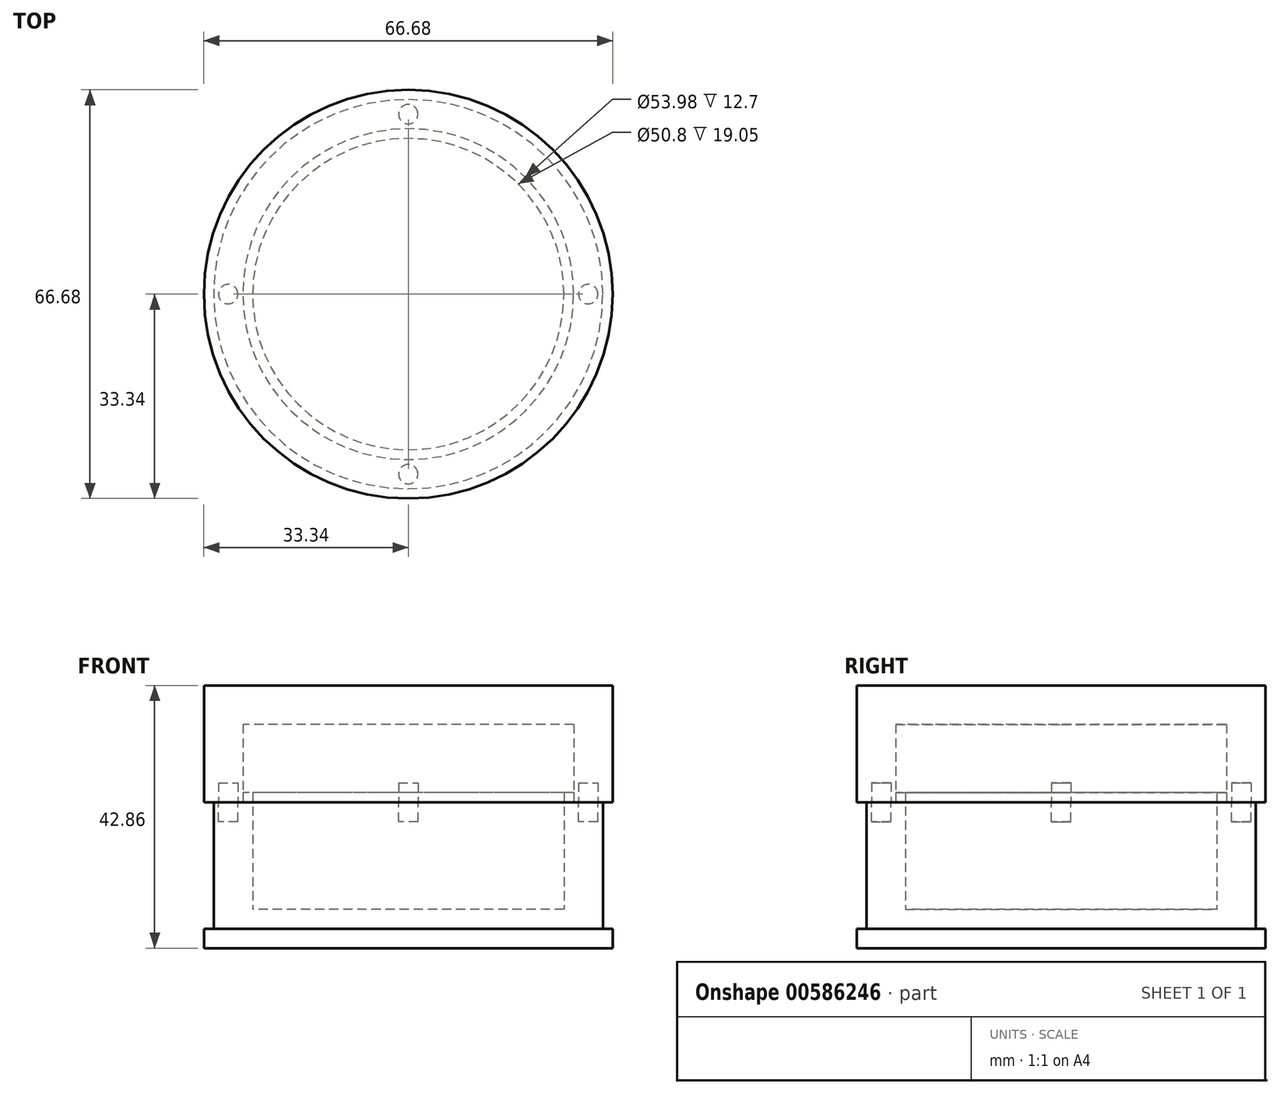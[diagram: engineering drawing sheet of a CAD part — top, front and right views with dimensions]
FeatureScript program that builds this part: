
annotation { "Feature Type Name" : "Feature", "Feature Type Description" : "" }
export const myFeature = defineFeature(function(context is Context, id is Id, definition is map)
    precondition{}
    {
        {
            var Q0;
            Q0=qCreatedBy(makeId("Top.planeOp"),FACE);
            var sketch = newSketch(context, id + "F0", { "sketchPlane" : qUnion([Q0])});
            skCircle(sketch, "E0", {"center": v(0, 0) * mm, "radius": 31.75 * mm});
            skCircle(sketch, "E1", {"center": v(0, 0) * mm, "radius": 33.34 * mm});
            skCircle(sketch, "E2", {"center": v(0, 0) * mm, "radius": 25.4 * mm});
            skSolve(sketch);
        }
        {
            var Q0;
            Q0=makeQuery(id+"F0.imprint","IMPRINT",FACE,{"disambiguationData":[TD([[makeQuery(id+"F0.imprint","IMPRINT",EDGE,{"derivedFrom":sQuery(id+"F0.wireOp",EDGE,"E2")}),1.0]])]});
            extrude(context, id + "F1", {"entities" : qUnion([Q0]), "depth" : 6.35 * mm, "offsetDistance" : 25.4 * mm});
        }
        {
            var Q0;
            Q0=makeQuery(id+"F0.imprint","IMPRINT",FACE,{"disambiguationData":[TD([[makeQuery(id+"F0.imprint","IMPRINT",EDGE,{"derivedFrom":sQuery(id+"F0.wireOp",EDGE,"E0")}),1.0]])]});
            extrude(context, id + "F2", {"entities" : qUnion([Q0]), "operationType" : NewBodyOperationType.ADD, "depth" : 23.8 * mm, "offsetDistance" : 25.4 * mm});
        }
        {
            var Q0;
            Q0=makeQuery(id+"F0.imprint","IMPRINT",FACE,{"disambiguationData":[TD([[makeQuery(id+"F0.imprint","IMPRINT",EDGE,{"derivedFrom":sQuery(id+"F0.wireOp",EDGE,"E0")}),-1.0]])]});
            extrude(context, id + "F3", {"entities" : qUnion([Q0]), "operationType" : NewBodyOperationType.ADD, "depth" : 3.17 * mm, "offsetDistance" : 25.4 * mm});
        }
        {
            var Q0;
            Q0=makeQuery(id+"F2.opExtrude","CAP_FACE",FACE,{"disambiguationData":[OSD([sQuery(id+"F0.wireOp",EDGE,"E0"),sQuery(id+"F0.wireOp",EDGE,"E2")])],"isStart":false});
            var sketch = newSketch(context, id + "F4", { "sketchPlane" : qUnion([Q0])});
            skCircle(sketch, "E3", {"center": v(0, 0) * mm, "radius": 26.99 * mm});
            skSolve(sketch);
        }
        {
            var Q0;
            Q0=makeQuery(id+"F4.imprint","IMPRINT",FACE,{"disambiguationData":[TD([[makeQuery(id+"F4.imprint","IMPRINT",EDGE,{"derivedFrom":sQuery(id+"F4.wireOp",EDGE,"E3")}),1.0]])]});
            extrude(context, id + "F5", {"entities" : qUnion([Q0]), "operationType" : NewBodyOperationType.ADD, "depth" : 1.59 * mm, "offsetDistance" : 25.4 * mm});
        }
        {
            var Q0;
            Q0=makeQuery(id+"F2.opExtrude","CAP_FACE",FACE,{"disambiguationData":[OSD([sQuery(id+"F0.wireOp",EDGE,"E0"),sQuery(id+"F0.wireOp",EDGE,"E2")])],"isStart":false});
            var sketch = newSketch(context, id + "F6", { "sketchPlane" : qUnion([Q0])});
            skLineSegment(sketch, "E4", {"start": v(0, -31.75) * mm, "end": v(0, -26.99) * mm, "construction": true});
            skLineSegment(sketch, "E5", {"start": v(0, 0) * mm, "end": v(31.75, 0) * mm, "construction": true});
            skCircle(sketch, "E6", {"center": v(0, -29.37) * mm, "radius": 1.59 * mm});
            skCircle(sketch, "E7.1.0", {"center": v(29.37, 0) * mm, "radius": 1.59 * mm});
            skCircle(sketch, "E7.2.0", {"center": v(0, 29.37) * mm, "radius": 1.59 * mm});
            skCircle(sketch, "E7.3.0", {"center": v(-29.37, 0) * mm, "radius": 1.59 * mm});
            skPoint(sketch, "E7.center", {"position": v(0, 0) * mm});
            skSolve(sketch);
        }
        {
            var Q0;
            Q0=makeQuery(id+"F6.imprint","IMPRINT",FACE,{"disambiguationData":[TD([[makeQuery(id+"F6.imprint","IMPRINT",EDGE,{"derivedFrom":sQuery(id+"F6.wireOp",EDGE,"E6")}),-1.0]])]});
            var sketch = newSketch(context, id + "F7", { "sketchPlane" : qUnion([Q0])});
            skCircle(sketch, "E8.0", {"center": v(0, 0) * mm, "radius": 33.34 * mm});
            skCircle(sketch, "E9.0", {"center": v(0, 0) * mm, "radius": 26.99 * mm});
            skSolve(sketch);
        }
        {
            var Q0;
            Q0 = qSketchRegion(id + "F7", true);
            extrude(context, id + "F8", {"entities" : qUnion([Q0]), "depth" : 9.52 * mm, "offsetDistance" : 25.4 * mm});
        }
        {
            var Q0;
            Q0=makeQuery(id+"F8.opExtrude","CAP_FACE",FACE,{"disambiguationData":[OSD([sQuery(id+"F7.wireOp",EDGE,"E8.0"),sQuery(id+"F7.wireOp",EDGE,"E9.0")])],"isStart":false});
            var sketch = newSketch(context, id + "F9", { "sketchPlane" : qUnion([Q0])});
            skCircle(sketch, "E10.0", {"center": v(0, 0) * mm, "radius": 33.34 * mm});
            skSolve(sketch);
        }
        {
            var Q0;
            Q0 = qSketchRegion(id + "F9", true);
            extrude(context, id + "F10", {"entities" : qUnion([Q0]), "operationType" : NewBodyOperationType.ADD, "depth" : 9.52 * mm, "offsetDistance" : 25.4 * mm});
        }
        {
            var Q0;
            Q0=makeQuery(id+"F8.opExtrude","CAP_FACE",FACE,{"disambiguationData":[OSD([sQuery(id+"F7.wireOp",EDGE,"E8.0"),sQuery(id+"F7.wireOp",EDGE,"E9.0")])],"isStart":true});
            var sketch = newSketch(context, id + "F11", { "sketchPlane" : qUnion([Q0])});
            skCircle(sketch, "E11.0", {"center": v(29.37, 0) * mm, "radius": 1.59 * mm});
            skCircle(sketch, "E12.0", {"center": v(0, -29.37) * mm, "radius": 1.59 * mm});
            skCircle(sketch, "E13.0", {"center": v(-29.37, 0) * mm, "radius": 1.59 * mm});
            skCircle(sketch, "E14.0", {"center": v(0, 29.37) * mm, "radius": 1.59 * mm});
            skSolve(sketch);
        }
        {
            var Q0;
            Q0 = qSketchRegion(id + "F11", true);
            extrude(context, id + "F12", {"entities" : qUnion([Q0]), "operationType" : NewBodyOperationType.REMOVE, "oppositeDirection" : true, "depth" : 3.17 * mm, "offsetDistance" : 25.4 * mm});
        }
        {
            var Q0;
            Q0=makeQuery(id+"F6.imprint","IMPRINT",FACE,{"disambiguationData":[TD([[makeQuery(id+"F6.imprint","IMPRINT",EDGE,{"derivedFrom":sQuery(id+"F6.wireOp",EDGE,"E7.1.0")}),1.0]])]});
            var Q1;
            Q1=makeQuery(id+"F6.imprint","IMPRINT",FACE,{"disambiguationData":[TD([[makeQuery(id+"F6.imprint","IMPRINT",EDGE,{"derivedFrom":sQuery(id+"F6.wireOp",EDGE,"E7.3.0")}),1.0]])]});
            var Q2;
            Q2=makeQuery(id+"F6.imprint","IMPRINT",FACE,{"disambiguationData":[TD([[makeQuery(id+"F6.imprint","IMPRINT",EDGE,{"derivedFrom":sQuery(id+"F6.wireOp",EDGE,"E7.2.0")}),1.0]])]});
            var Q3;
            Q3=makeQuery(id+"F6.imprint","IMPRINT",FACE,{"disambiguationData":[TD([[makeQuery(id+"F6.imprint","IMPRINT",EDGE,{"derivedFrom":sQuery(id+"F6.wireOp",EDGE,"E6")}),1.0]])]});
            extrude(context, id + "F13", {"entities" : qUnion([Q0, Q1, Q2, Q3]), "operationType" : NewBodyOperationType.REMOVE, "oppositeDirection" : true, "depth" : 3.17 * mm, "offsetDistance" : 25.4 * mm});
        }
        {
            var Q0;
            Q0=makeQuery(id+"F10.opExtrude","CAP_FACE",FACE,{"disambiguationData":[OSD([sQuery(id+"F9.wireOp",EDGE,"E10.0")])],"isStart":true});
            extrude(context, id + "F14", {"entities" : qUnion([Q0]), "operationType" : NewBodyOperationType.REMOVE, "oppositeDirection" : true, "depth" : 3.17 * mm, "offsetDistance" : 25.4 * mm});
        }
    });
